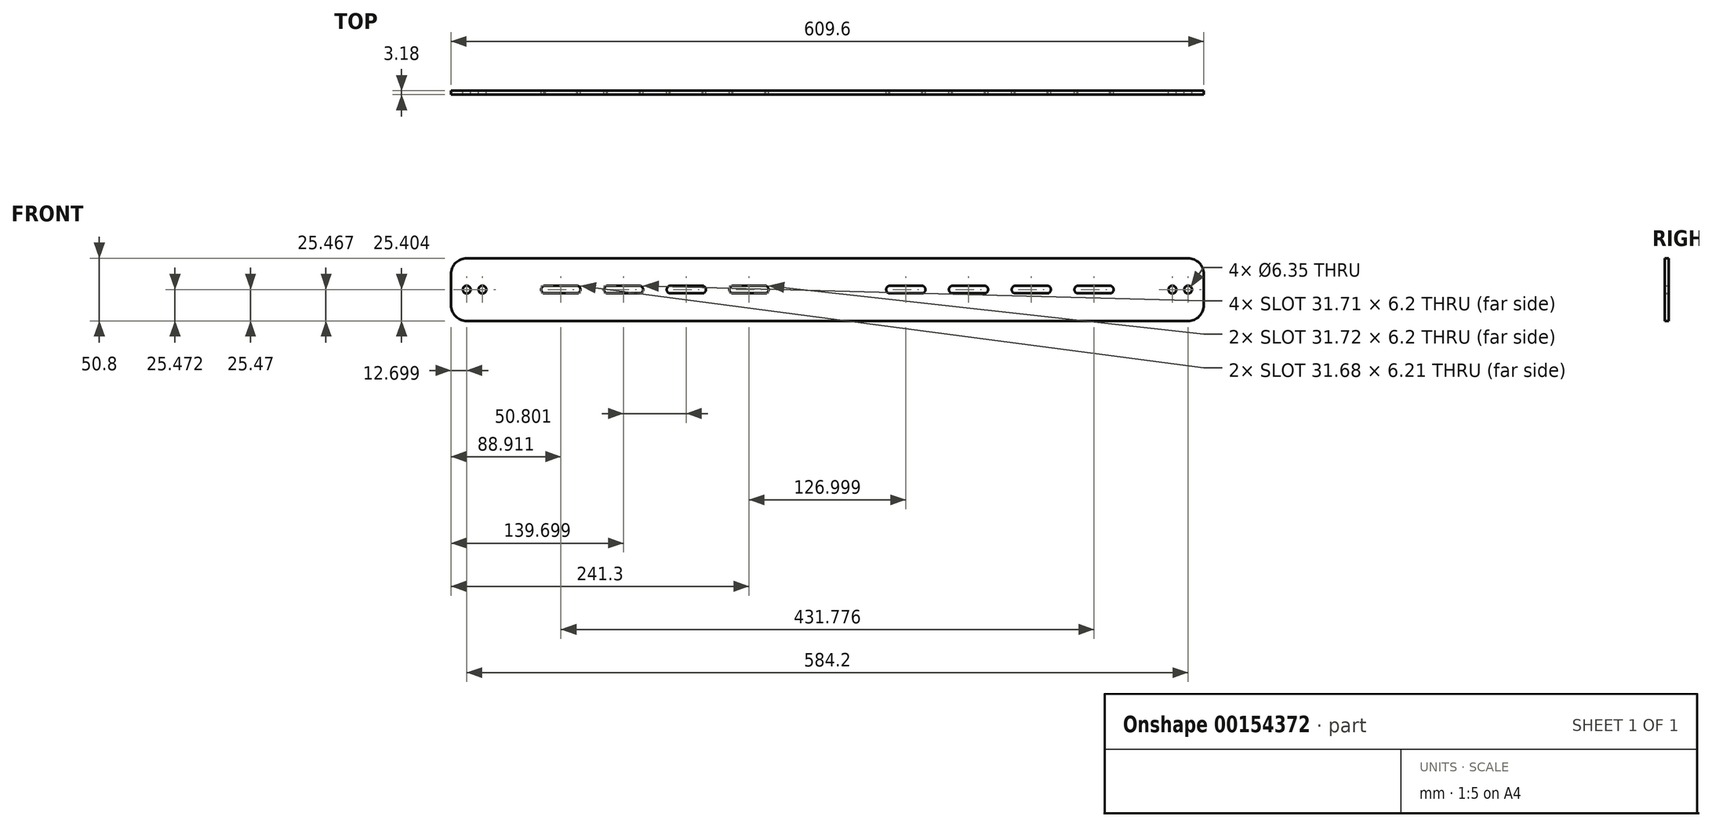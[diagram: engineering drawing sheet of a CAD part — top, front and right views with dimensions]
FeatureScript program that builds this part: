
annotation { "Feature Type Name" : "Feature", "Feature Type Description" : "" }
export const myFeature = defineFeature(function(context is Context, id is Id, definition is map)
    precondition{}
    {
        {
            var Q0;
            Q0=qCreatedBy(makeId("Front.planeOp"),FACE);
            var sketch = newSketch(context, id + "F0", { "sketchPlane" : qUnion([Q0])});
            skLineSegment(sketch, "E0.bottom", {"start": v(-497.96, 52.87) * mm, "end": v(-205.86, 52.87) * mm});
            skLineSegment(sketch, "E0.top", {"start": v(-497.96, 2.07) * mm, "end": v(-205.86, 2.07) * mm});
            skLineSegment(sketch, "E0.left", {"start": v(-510.66, 40.17) * mm, "end": v(-510.66, 14.77) * mm});
            skArc(sketch, "E1.filletArc", {"start": v(-497.96, 52.87) * mm, "mid": v(-506.94, 49.15) * mm, "end": v(-510.66, 40.17) * mm});
            skArc(sketch, "E2.filletArc", {"start": v(-510.66, 14.77) * mm, "mid": v(-506.94, 5.8) * mm, "end": v(-497.96, 2.07) * mm});
            skCircle(sketch, "E3", {"center": v(-497.96, 27.47) * mm, "radius": 3.18 * mm});
            skCircle(sketch, "E4", {"center": v(-485.26, 27.47) * mm, "radius": 3.18 * mm});
            skLineSegment(sketch, "E5", {"start": v(-459.86, 52.87) * mm, "end": v(-459.86, 2.07) * mm});
            skLineSegment(sketch, "E6", {"start": v(-434.46, 30.65) * mm, "end": v(-434.46, 30.65) * mm});
            skLineSegment(sketch, "E7", {"start": v(-205.86, 52.87) * mm, "end": v(-205.86, 2.07) * mm});
            skLineSegment(sketch, "E8", {"start": v(-433.53, 24.44) * mm, "end": v(-408.13, 24.44) * mm});
            skArc(sketch, "E9", {"start": v(-434.31, 30.65) * mm, "mid": v(-437.59, 28.02) * mm, "end": v(-435.39, 24.44) * mm});
            skArc(sketch, "E10", {"start": v(-408.13, 24.44) * mm, "mid": v(-405.9, 27.85) * mm, "end": v(-408.88, 30.64) * mm});
            skArc(sketch, "E11", {"start": v(-357.33, 24.44) * mm, "mid": v(-355.1, 27.83) * mm, "end": v(-358.03, 30.64) * mm});
            skLineSegment(sketch, "E12.trimOffspring", {"start": v(-408.88, 30.64) * mm, "end": v(-434.31, 30.65) * mm});
            skLineSegment(sketch, "E13.trimOffspring", {"start": v(-384.59, 24.44) * mm, "end": v(-357.33, 24.44) * mm});
            skLineSegment(sketch, "E14", {"start": v(-307.46, 30.65) * mm, "end": v(-307.46, 30.64) * mm});
            skLineSegment(sketch, "E15.trimOffspring", {"start": v(-333.79, 24.44) * mm, "end": v(-306.53, 24.44) * mm});
            skLineSegment(sketch, "E16.trimOffspring", {"start": v(-358.03, 30.64) * mm, "end": v(-383.87, 30.64) * mm});
            skLineSegment(sketch, "E17.trimOffspring", {"start": v(-307.19, 30.64) * mm, "end": v(-333.11, 30.64) * mm});
            skLineSegment(sketch, "E18.trimOffspring", {"start": v(-282.99, 24.44) * mm, "end": v(-255.73, 24.44) * mm});
            skArc(sketch, "E19.trimOffspring", {"start": v(-306.53, 24.44) * mm, "mid": v(-304.3, 27.8) * mm, "end": v(-307.19, 30.64) * mm});
            skArc(sketch, "E20.trimOffspring", {"start": v(-333.11, 30.64) * mm, "mid": v(-336.02, 27.82) * mm, "end": v(-333.79, 24.44) * mm});
            skLineSegment(sketch, "E21", {"start": v(-433.53, 24.44) * mm, "end": v(-435.39, 24.44) * mm});
            skArc(sketch, "E22.trimOffspring", {"start": v(-383.87, 30.64) * mm, "mid": v(-386.81, 27.84) * mm, "end": v(-384.59, 24.44) * mm});
            skArc(sketch, "E23.trimOffspring", {"start": v(-282.35, 30.64) * mm, "mid": v(-285.22, 27.8) * mm, "end": v(-282.99, 24.44) * mm});
            skLineSegment(sketch, "E24.trimOffspring", {"start": v(-256.35, 30.63) * mm, "end": v(-282.35, 30.64) * mm});
            skArc(sketch, "E25.trimOffspring", {"start": v(-255.73, 24.44) * mm, "mid": v(-253.5, 27.79) * mm, "end": v(-256.35, 30.63) * mm});
            skLineSegment(sketch, "E26.MirrorCS", {"start": v(22.74, 30.65) * mm, "end": v(22.74, 30.65) * mm});
            skLineSegment(sketch, "E27.MirrorCS", {"start": v(-104.26, 30.65) * mm, "end": v(-104.26, 30.64) * mm});
            skArc(sketch, "E28.MirrorCS", {"start": v(22.6, 30.65) * mm, "mid": v(25.87, 28.02) * mm, "end": v(23.67, 24.44) * mm});
            skArc(sketch, "E29.MirrorCS", {"start": v(-105.19, 24.44) * mm, "mid": v(-107.42, 27.8) * mm, "end": v(-104.54, 30.64) * mm});
            skArc(sketch, "E30.MirrorCS", {"start": v(-3.59, 24.44) * mm, "mid": v(-5.81, 27.85) * mm, "end": v(-2.84, 30.64) * mm});
            skArc(sketch, "E31.MirrorCS", {"start": v(-54.39, 24.44) * mm, "mid": v(-56.61, 27.83) * mm, "end": v(-53.7, 30.64) * mm});
            skArc(sketch, "E32.MirrorCS", {"start": v(-155.99, 24.44) * mm, "mid": v(-158.22, 27.79) * mm, "end": v(-155.37, 30.63) * mm});
            skArc(sketch, "E33.MirrorCS", {"start": v(-78.6, 30.64) * mm, "mid": v(-75.7, 27.82) * mm, "end": v(-77.93, 24.44) * mm});
            skArc(sketch, "E34.MirrorCS", {"start": v(-129.37, 30.64) * mm, "mid": v(-126.5, 27.8) * mm, "end": v(-128.73, 24.44) * mm});
            skArc(sketch, "E35.MirrorCS", {"start": v(-27.85, 30.64) * mm, "mid": v(-24.9, 27.84) * mm, "end": v(-27.13, 24.44) * mm});
            skLineSegment(sketch, "E36.MirrorCS", {"start": v(21.81, 24.44) * mm, "end": v(23.67, 24.44) * mm});
            skLineSegment(sketch, "E37.MirrorCS", {"start": v(-27.13, 24.44) * mm, "end": v(-54.39, 24.44) * mm});
            skLineSegment(sketch, "E38.MirrorCS", {"start": v(-155.37, 30.63) * mm, "end": v(-129.37, 30.64) * mm});
            skLineSegment(sketch, "E39.MirrorCS", {"start": v(86.24, 2.07) * mm, "end": v(-205.86, 2.07) * mm});
            skLineSegment(sketch, "E40.MirrorCS", {"start": v(-2.84, 30.64) * mm, "end": v(22.6, 30.65) * mm});
            skLineSegment(sketch, "E41.MirrorCS", {"start": v(48.14, 52.87) * mm, "end": v(48.14, 2.07) * mm});
            skLineSegment(sketch, "E42.MirrorCS", {"start": v(21.81, 24.44) * mm, "end": v(-3.59, 24.44) * mm});
            skCircle(sketch, "E43.MirrorC", {"center": v(86.24, 27.47) * mm, "radius": 3.18 * mm});
            skLineSegment(sketch, "E44.MirrorCS", {"start": v(-77.93, 24.44) * mm, "end": v(-105.19, 24.44) * mm});
            skLineSegment(sketch, "E45.MirrorCS", {"start": v(-128.73, 24.44) * mm, "end": v(-155.99, 24.44) * mm});
            skLineSegment(sketch, "E46.MirrorCS", {"start": v(-53.7, 30.64) * mm, "end": v(-27.85, 30.64) * mm});
            skArc(sketch, "E47.MirrorCS", {"start": v(98.94, 14.77) * mm, "mid": v(95.22, 5.8) * mm, "end": v(86.24, 2.07) * mm});
            skCircle(sketch, "E48.MirrorC", {"center": v(73.54, 27.47) * mm, "radius": 3.18 * mm});
            skArc(sketch, "E49.MirrorCS", {"start": v(86.24, 52.87) * mm, "mid": v(95.22, 49.15) * mm, "end": v(98.94, 40.17) * mm});
            skLineSegment(sketch, "E50.MirrorCS", {"start": v(86.24, 52.87) * mm, "end": v(-205.86, 52.87) * mm});
            skLineSegment(sketch, "E51.MirrorCS", {"start": v(98.94, 40.17) * mm, "end": v(98.94, 14.77) * mm});
            skLineSegment(sketch, "E52.MirrorCS", {"start": v(-104.54, 30.64) * mm, "end": v(-78.6, 30.64) * mm});
            skSolve(sketch);
        }
        {
            var Q0;
            Q0 = qSketchRegion(id + "F0", true);
            extrude(context, id + "F1", {"entities" : qUnion([Q0]), "depth" : 3.17 * mm});
        }
    });
